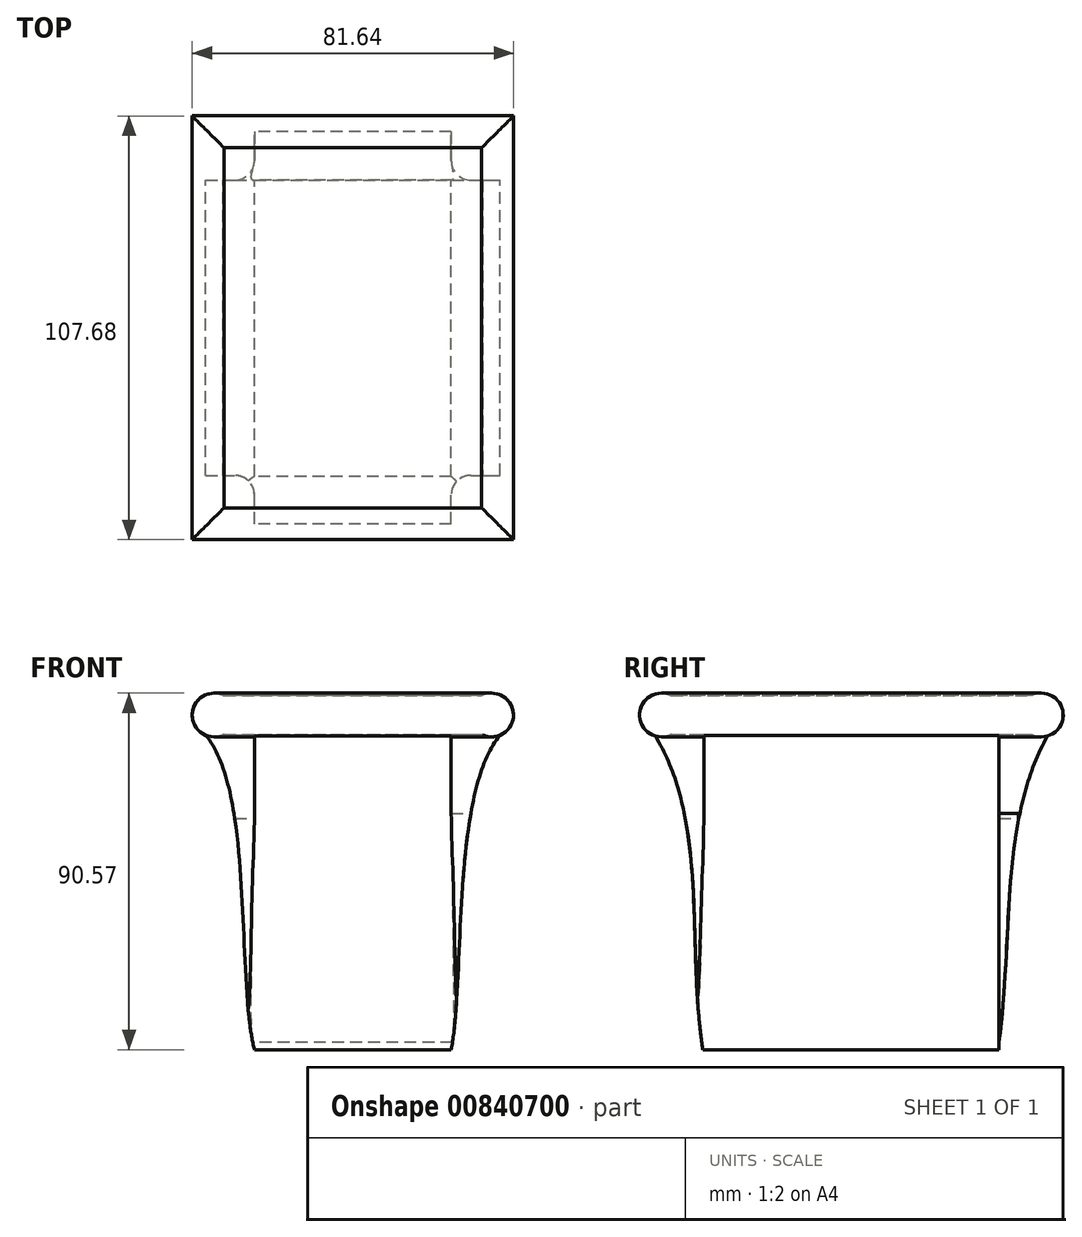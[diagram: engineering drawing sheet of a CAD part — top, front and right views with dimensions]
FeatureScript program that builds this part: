
annotation { "Feature Type Name" : "Feature", "Feature Type Description" : "" }
export const myFeature = defineFeature(function(context is Context, id is Id, definition is map)
    precondition{}
    {
        {
            var Q0;
            Q0=qCreatedBy(makeId("Front.planeOp"),FACE);
            var sketch = newSketch(context, id + "F0", { "sketchPlane" : qUnion([Q0])});
            skLineSegment(sketch, "E0.bottom", {"start": v(-25, 0) * mm, "end": v(25, 0) * mm});
            skLineSegment(sketch, "E0.top", {"start": v(-25, 80) * mm, "end": v(25, 80) * mm});
            skLineSegment(sketch, "E1", {"start": v(-37.5, 80) * mm, "end": v(37.5, 80) * mm});
            skFitSpline(sketch, "E2", {"points": [v(-37.5, 80) * mm, v(-25, 0) * mm], "startDerivative": vector(37.5, -43.44) * mm, "endDerivative": vector(13.99, -54.98) * mm});
            skFitSpline(sketch, "E3", {"points": [v(25, 0) * mm, v(37.5, 80) * mm], "startDerivative": vector(10.53, 54.98) * mm, "endDerivative": vector(37.5, 43.44) * mm});
            skSolve(sketch);
        }
        {
            var Q0;
            Q0=qSketchRegion(id+"F0",true);
            extrude(context, id + "F1", {"entities" : qUnion([Q0]), "depth" : 37.5 * mm, "offsetDistance" : 25 * mm, "hasSecondDirection" : true, "secondDirectionOppositeDirection" : true, "secondDirectionDepth" : 37.5 * mm});
        }
        {
            var Q0;
            Q0=qCreatedBy(makeId("Right.planeOp"),FACE);
            var sketch = newSketch(context, id + "F2", { "sketchPlane" : qUnion([Q0])});
            skLineSegment(sketch, "E4", {"start": v(-50, 80) * mm, "end": v(50, 80) * mm});
            skFitSpline(sketch, "E5", {"points": [v(-50, 80) * mm, v(-37.75, 0) * mm], "startDerivative": vector(41.46, -67.14) * mm, "endDerivative": vector(12.51, -80.09) * mm});
            skFitSpline(sketch, "E6", {"points": [v(50, 80) * mm, v(37.23, 0) * mm], "startDerivative": vector(-38.32, -67.14) * mm, "endDerivative": vector(-12.25, -80.09) * mm});
            skLineSegment(sketch, "E7", {"start": v(-37.75, 0) * mm, "end": v(37.23, 0) * mm});
            skSolve(sketch);
        }
        {
            var Q0;
            Q0=qSketchRegion(id+"F2",true);
            extrude(context, id + "F3", {"entities" : qUnion([Q0]), "operationType" : NewBodyOperationType.ADD, "depth" : 25 * mm, "offsetDistance" : 25 * mm, "hasSecondDirection" : true, "secondDirectionOppositeDirection" : true, "secondDirectionDepth" : 25 * mm});
        }
        {
            var Q0;
            Q0=makeQuery(id+"F3.boolean.opBoolean","INTERSECT",EDGE,{"derivedFrom":[makeQuery(id+"F1.opExtrude","CAP_FACE",FACE,{"disambiguationData":[OSD([sQuery(id+"F0.wireOp",EDGE,"E0.bottom"),sQuery(id+"F0.wireOp",EDGE,"E1"),sQuery(id+"F0.wireOp",EDGE,"E2"),sQuery(id+"F0.wireOp",EDGE,"E3")])],"isStart":false}),makeQuery(id+"F3.opExtrude","CAP_FACE",FACE,{"disambiguationData":[OSD([sQuery(id+"F2.wireOp",EDGE,"E4"),sQuery(id+"F2.wireOp",EDGE,"E5"),sQuery(id+"F2.wireOp",EDGE,"E6"),sQuery(id+"F2.wireOp",EDGE,"E7")])],"isStart":true})]});
            var Q1;
            Q1=makeQuery(id+"F3.boolean.opBoolean","INTERSECT",EDGE,{"derivedFrom":[makeQuery(id+"F1.opExtrude","CAP_FACE",FACE,{"disambiguationData":[OSD([sQuery(id+"F0.wireOp",EDGE,"E0.bottom"),sQuery(id+"F0.wireOp",EDGE,"E1"),sQuery(id+"F0.wireOp",EDGE,"E2"),sQuery(id+"F0.wireOp",EDGE,"E3")])],"isStart":false}),makeQuery(id+"F3.opExtrude","CAP_FACE",FACE,{"disambiguationData":[OSD([sQuery(id+"F2.wireOp",EDGE,"E4"),sQuery(id+"F2.wireOp",EDGE,"E5"),sQuery(id+"F2.wireOp",EDGE,"E6"),sQuery(id+"F2.wireOp",EDGE,"E7")])],"isStart":false})]});
            var Q2;
            Q2=makeQuery(id+"F3.boolean.opBoolean","INTERSECT",EDGE,{"derivedFrom":[makeQuery(id+"F1.opExtrude","CAP_FACE",FACE,{"disambiguationData":[OSD([sQuery(id+"F0.wireOp",EDGE,"E0.bottom"),sQuery(id+"F0.wireOp",EDGE,"E1"),sQuery(id+"F0.wireOp",EDGE,"E2"),sQuery(id+"F0.wireOp",EDGE,"E3")])],"isStart":true}),makeQuery(id+"F3.opExtrude","CAP_FACE",FACE,{"disambiguationData":[OSD([sQuery(id+"F2.wireOp",EDGE,"E4"),sQuery(id+"F2.wireOp",EDGE,"E5"),sQuery(id+"F2.wireOp",EDGE,"E6"),sQuery(id+"F2.wireOp",EDGE,"E7")])],"isStart":false})]});
            var Q3;
            Q3=makeQuery(id+"F3.boolean.opBoolean","INTERSECT",EDGE,{"derivedFrom":[makeQuery(id+"F1.opExtrude","CAP_FACE",FACE,{"disambiguationData":[OSD([sQuery(id+"F0.wireOp",EDGE,"E0.bottom"),sQuery(id+"F0.wireOp",EDGE,"E1"),sQuery(id+"F0.wireOp",EDGE,"E2"),sQuery(id+"F0.wireOp",EDGE,"E3")])],"isStart":true}),makeQuery(id+"F3.opExtrude","CAP_FACE",FACE,{"disambiguationData":[OSD([sQuery(id+"F2.wireOp",EDGE,"E4"),sQuery(id+"F2.wireOp",EDGE,"E5"),sQuery(id+"F2.wireOp",EDGE,"E6"),sQuery(id+"F2.wireOp",EDGE,"E7")])],"isStart":true})]});
            fillet(context, id + "F4", {"entities" : qUnion([Q0, Q1, Q2, Q3]), "radius" : 5 * mm, "tangentPropagation" : true, "allowEdgeOverflow" : false});
        }
        {
            var Q0;
            Q0=makeQuery(id+"F3.boolean.opBoolean","MERGE",FACE,{"derivedFrom":[makeQuery(id+"F1.opExtrude","SWEPT_FACE",FACE,{"disambiguationData":[OSD([sQuery(id+"F0.wireOp",EDGE,"E1")])]}),makeQuery(id+"F3.opExtrude","SWEPT_FACE",FACE,{"disambiguationData":[OSD([sQuery(id+"F2.wireOp",EDGE,"E4")])]})]});
            var sketch = newSketch(context, id + "F5", { "sketchPlane" : qUnion([Q0])});
            skLineSegment(sketch, "E8.bottom", {"start": v(32.74, 45.76) * mm, "end": v(-32.74, 45.76) * mm});
            skLineSegment(sketch, "E8.top", {"start": v(32.74, -45.76) * mm, "end": v(-32.74, -45.76) * mm});
            skLineSegment(sketch, "E8.left", {"start": v(32.74, 45.76) * mm, "end": v(32.74, -45.76) * mm});
            skLineSegment(sketch, "E8.right", {"start": v(-32.74, 45.76) * mm, "end": v(-32.74, -45.76) * mm});
            skPoint(sketch, "E8.middle", {"position": v(0, 0) * mm});
            skSolve(sketch);
        }
        {
            var Q0;
            Q0=qSketchRegion(id+"F5",true);
            extrude(context, id + "F6", {"entities" : qUnion([Q0]), "operationType" : NewBodyOperationType.ADD, "depth" : 10 * mm, "offsetDistance" : 25 * mm});
        }
        {
            var Q0;
            Q0=qCreatedBy(makeId("Top.planeOp"),FACE);
            cPlane(context, id + "F7", {"entities" : qUnion([Q0]), "cplaneType" : CPlaneType.OFFSET, "offset" : 85 * mm, "width" : 150 * mm, "height" : 150 * mm});
        }
        {
            var Q0;
            Q0=qCreatedBy(makeId("Front.planeOp"),FACE);
            var sketch = newSketch(context, id + "F8", { "sketchPlane" : qUnion([Q0])});
            skCircle(sketch, "E9", {"center": v(35.27, 85.02) * mm, "radius": 5.55 * mm});
            skSolve(sketch);
        }
        {
            var Q0;
            Q0=makeQuery(id+"F8.imprint","IMPRINT",FACE,{"disambiguationData":[TD([[makeQuery(id+"F8.imprint","IMPRINT",EDGE,{"derivedFrom":sQuery(id+"F8.wireOp",EDGE,"E9")}),1.0]])]});
            var Q1;
            Q1=makeQuery(id+"F6.opExtrude","CAP_EDGE",EDGE,{"disambiguationData":[OSD([sQuery(id+"F5.wireOp",EDGE,"E8.left")])],"isStart":false});
            var Q2;
            Q2=makeQuery(id+"F6.opExtrude","CAP_EDGE",EDGE,{"disambiguationData":[OSD([sQuery(id+"F5.wireOp",EDGE,"E8.bottom")])],"isStart":false});
            var Q3;
            Q3=makeQuery(id+"F6.opExtrude","CAP_EDGE",EDGE,{"disambiguationData":[OSD([sQuery(id+"F5.wireOp",EDGE,"E8.right")])],"isStart":false});
            var Q4;
            Q4=makeQuery(id+"F6.opExtrude","CAP_EDGE",EDGE,{"disambiguationData":[OSD([sQuery(id+"F5.wireOp",EDGE,"E8.top")])],"isStart":false});
            sweep(context, id + "F9", {"operationType" : NewBodyOperationType.ADD, "profiles" : qUnion([Q0]), "path" : qUnion([Q1, Q2, Q3, Q4])});
        }
    });
